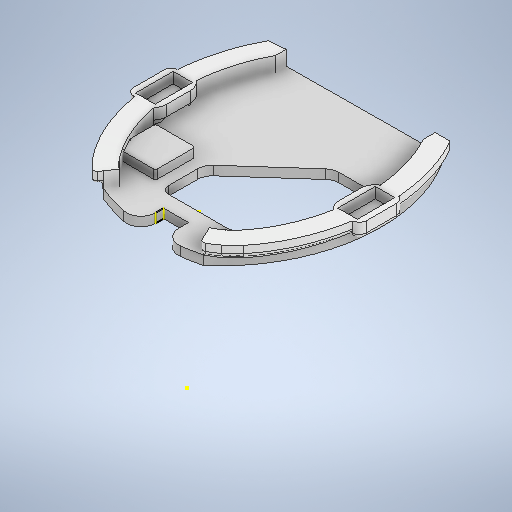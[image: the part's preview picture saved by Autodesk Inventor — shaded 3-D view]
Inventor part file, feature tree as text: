
AUTODESK INVENTOR PART (.ipt)
format: ipt  version: 2025.2 (Build 292293000, 293)  size: 771,072 bytes
history: native  units: in
note: dims shown in document units (in); Inventor stores cm internally (conversion verified against a paired STEP export)
features: fillet x18, sketch x11, extrude x9, other x3, projected_geometry x3
ambient origin geometry x8: Origin, YZ Plane, XZ Plane, XY Plane, X Axis, Y Axis, Z Axis, Center Point
bodies: Solid1 (feature_tree), Solid2 (feature_tree)
feature tree (44):
  other  "rat_cap_EC_v12.iam"
  other  "rat_cap_walls_v8.iam:1::rat_cap_left_wall_v8.ipt:1"
  other  "rat_cap_walls_v8.iam:1::rat_cap_right_wall_v8.ipt:1"
  extrude  "Extrusion1"  Depth=0.05in TaperAngle=0.0deg
  sketch  "Sketch3"  dims[d9=0.0812in d10=0.0in d11=0.0787in d12=0.0787in d16=0.315in]
  extrude  "Extrusion3"  Depth=0.0787in
  fillet  "Fillet3"  Radius=0.0787in
  fillet  "Fillet4"  Radius=0.315in
  extrude  "Extrusion4"  Depth=0.0812in TaperAngle=0.0deg
  extrude  "Extrusion5"  Depth=0.0787in
  fillet  "Fillet5"  Radius=0.2165in
  fillet  "Fillet6"  Radius=0.2165in
  extrude  "Extrusion13"  Depth=0.0787in
  fillet  "Fillet7"  Radius=0.0787in
  fillet  "Fillet8"  Radius=0.0787in
  fillet  "Fillet10"  Radius=0.0787in
  fillet  "Fillet11"  Radius=0.0394in
  fillet  "Fillet12"  Radius=0.0118in
  fillet  "Fillet13"  Radius=0.0118in
  fillet  "Fillet14"  Radius=0.0118in
  fillet  "Fillet15"  Radius=0.0118in
  fillet  "Fillet16"  Radius=0.2047in
  extrude  "Extrusion14"  Depth=0.0591in TaperAngle=0.0deg
  extrude  "Extrusion15"  Depth=0.0787in
  sketch  "Sketch17"  dims[d33=0.0197in d34=0.0344in]
  extrude  "Extrusion16"  Depth=0.0394in
  fillet  "Fillet17"  Radius=0.0394in
  fillet  "Fillet18"  Radius=0.0118in
  fillet  "Fillet19"  Radius=0.0118in
  fillet  "Fillet20"  Radius=0.0118in
  fillet  "Fillet21"  Radius=0.0197in
  extrude  "Extrusion17"  Depth=0.0344in
  sketch  "Sketch1"  dims[d0=0.3937in d1=0.05in d2=0.0in]
  sketch  "Sketch4"  dims[d17=0.0812in d18=0.0in d19=0.0812in d20=0.0in]
  projected_geometry  "Projected Loop1"
  sketch  "Sketch5"  dims[d42=0.0787in d43=0.0787in d44=0.2165in d45=0.2165in]
  sketch  "Sketch6"  dims[d46=0.0984in d47=0.0in d48=0.0787in d49=0.0787in d51=0.0787in d52=0.0787in d53=0.0394in d54=0.0118in d55=0.0118in d56=0.0118in d57=0.0118in d58=0.2047in]
  sketch  "Sketch14"  dims[d59=0.2047in d60=0.0591in d61=0.0in]
  sketch  "Sketch15"  dims[d62=0.0591in d63=0.0in d64=0.0787in]
  projected_geometry  "Projected Loop2"
  projected_geometry  "Projected Loop3"
  sketch  "Sketch16"  dims[d65=0.3878in d66=0.0in d67=0.0394in d68=0.0394in d69=0.0118in d70=0.0118in d71=0.0118in d72=0.0197in d73=0.0in]
  sketch  "Sketch18"  dims[d35=0.0197in]
  sketch  "Sketch19"  dims[d36=0.0344in]
